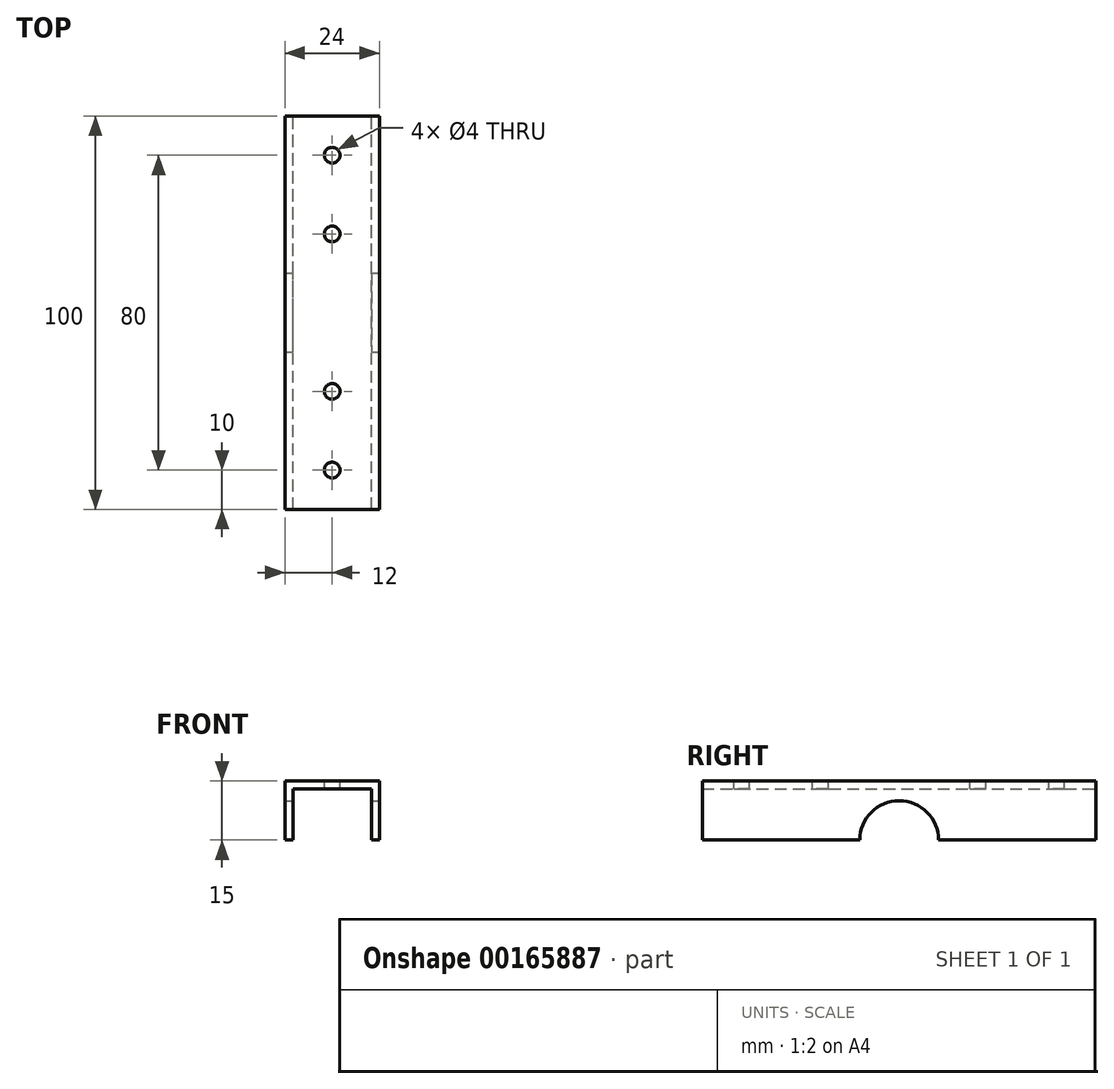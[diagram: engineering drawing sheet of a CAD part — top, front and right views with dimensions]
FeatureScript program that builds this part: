
annotation { "Feature Type Name" : "Feature", "Feature Type Description" : "" }
export const myFeature = defineFeature(function(context is Context, id is Id, definition is map)
    precondition{}
    {
        {
            var Q0;
            Q0=qCreatedBy(makeId("Front.planeOp"),FACE);
            var sketch = newSketch(context, id + "F0", { "sketchPlane" : qUnion([Q0])});
            skLineSegment(sketch, "E0", {"start": v(0, 0) * mm, "end": v(-24, 0) * mm});
            skLineSegment(sketch, "E1", {"start": v(-24, 0) * mm, "end": v(-24, -15) * mm});
            skLineSegment(sketch, "E2", {"start": v(-22, -15) * mm, "end": v(-24, -15) * mm});
            skLineSegment(sketch, "E3", {"start": v(-22, -15) * mm, "end": v(-22, -2) * mm});
            skLineSegment(sketch, "E4", {"start": v(-22, -2) * mm, "end": v(-2, -2) * mm});
            skLineSegment(sketch, "E5", {"start": v(-2, -2) * mm, "end": v(-2, -15) * mm});
            skLineSegment(sketch, "E6", {"start": v(-2, -15) * mm, "end": v(0, -15) * mm});
            skLineSegment(sketch, "E7", {"start": v(0, -15) * mm, "end": v(0, 0) * mm});
            skSolve(sketch);
        }
        {
            var Q0;
            Q0=makeQuery(id+"F0.imprint","IMPRINT",FACE,{"disambiguationData":[TD([[makeQuery(id+"F0.imprint","IMPRINT",EDGE,{"derivedFrom":sQuery(id+"F0.wireOp",EDGE,"E0")}),1.0]])]});
            extrude(context, id + "F1", {"entities" : qUnion([Q0]), "depth" : 100 * mm});
        }
        {
            var Q0;
            Q0=makeQuery(id+"F1.opExtrude","SWEPT_FACE",FACE,{"disambiguationData":[OSD([sQuery(id+"F0.wireOp",EDGE,"E7")])]});
            var sketch = newSketch(context, id + "F2", { "sketchPlane" : qUnion([Q0])});
            skCircle(sketch, "E8", {"center": v(-50, -15) * mm, "radius": 10 * mm});
            skSolve(sketch);
        }
        {
            var Q0;
            Q0 = qSketchRegion(id + "F2", true);
            extrude(context, id + "F3", {"entities" : qUnion([Q0]), "operationType" : NewBodyOperationType.REMOVE, "oppositeDirection" : true, "depth" : 25 * mm});
        }
        {
            var Q0;
            Q0=makeQuery(id+"F1.opExtrude","SWEPT_FACE",FACE,{"disambiguationData":[OSD([sQuery(id+"F0.wireOp",EDGE,"E0")])]});
            var sketch = newSketch(context, id + "F4", { "sketchPlane" : qUnion([Q0])});
            skCircle(sketch, "E9", {"center": v(-12, -90) * mm, "radius": 2 * mm});
            skCircle(sketch, "E10", {"center": v(-12, -10) * mm, "radius": 2 * mm});
            skCircle(sketch, "E11", {"center": v(-12, -70) * mm, "radius": 2 * mm});
            skCircle(sketch, "E12", {"center": v(-12, -30) * mm, "radius": 2 * mm});
            skSolve(sketch);
        }
        {
            var Q0;
            Q0=makeQuery(id+"F4.imprint","IMPRINT",FACE,{"disambiguationData":[TD([[makeQuery(id+"F4.imprint","IMPRINT",EDGE,{"derivedFrom":sQuery(id+"F4.wireOp",EDGE,"E9")}),1.0]])]});
            var Q1;
            Q1=makeQuery(id+"F4.imprint","IMPRINT",FACE,{"disambiguationData":[TD([[makeQuery(id+"F4.imprint","IMPRINT",EDGE,{"derivedFrom":sQuery(id+"F4.wireOp",EDGE,"E11")}),1.0]])]});
            var Q2;
            Q2=makeQuery(id+"F4.imprint","IMPRINT",FACE,{"disambiguationData":[TD([[makeQuery(id+"F4.imprint","IMPRINT",EDGE,{"derivedFrom":sQuery(id+"F4.wireOp",EDGE,"E12")}),1.0]])]});
            var Q3;
            Q3=makeQuery(id+"F4.imprint","IMPRINT",FACE,{"disambiguationData":[TD([[makeQuery(id+"F4.imprint","IMPRINT",EDGE,{"derivedFrom":sQuery(id+"F4.wireOp",EDGE,"E10")}),1.0]])]});
            extrude(context, id + "F5", {"entities" : qUnion([Q0, Q1, Q2, Q3]), "operationType" : NewBodyOperationType.REMOVE, "oppositeDirection" : true, "depth" : 25 * mm});
        }
    });
